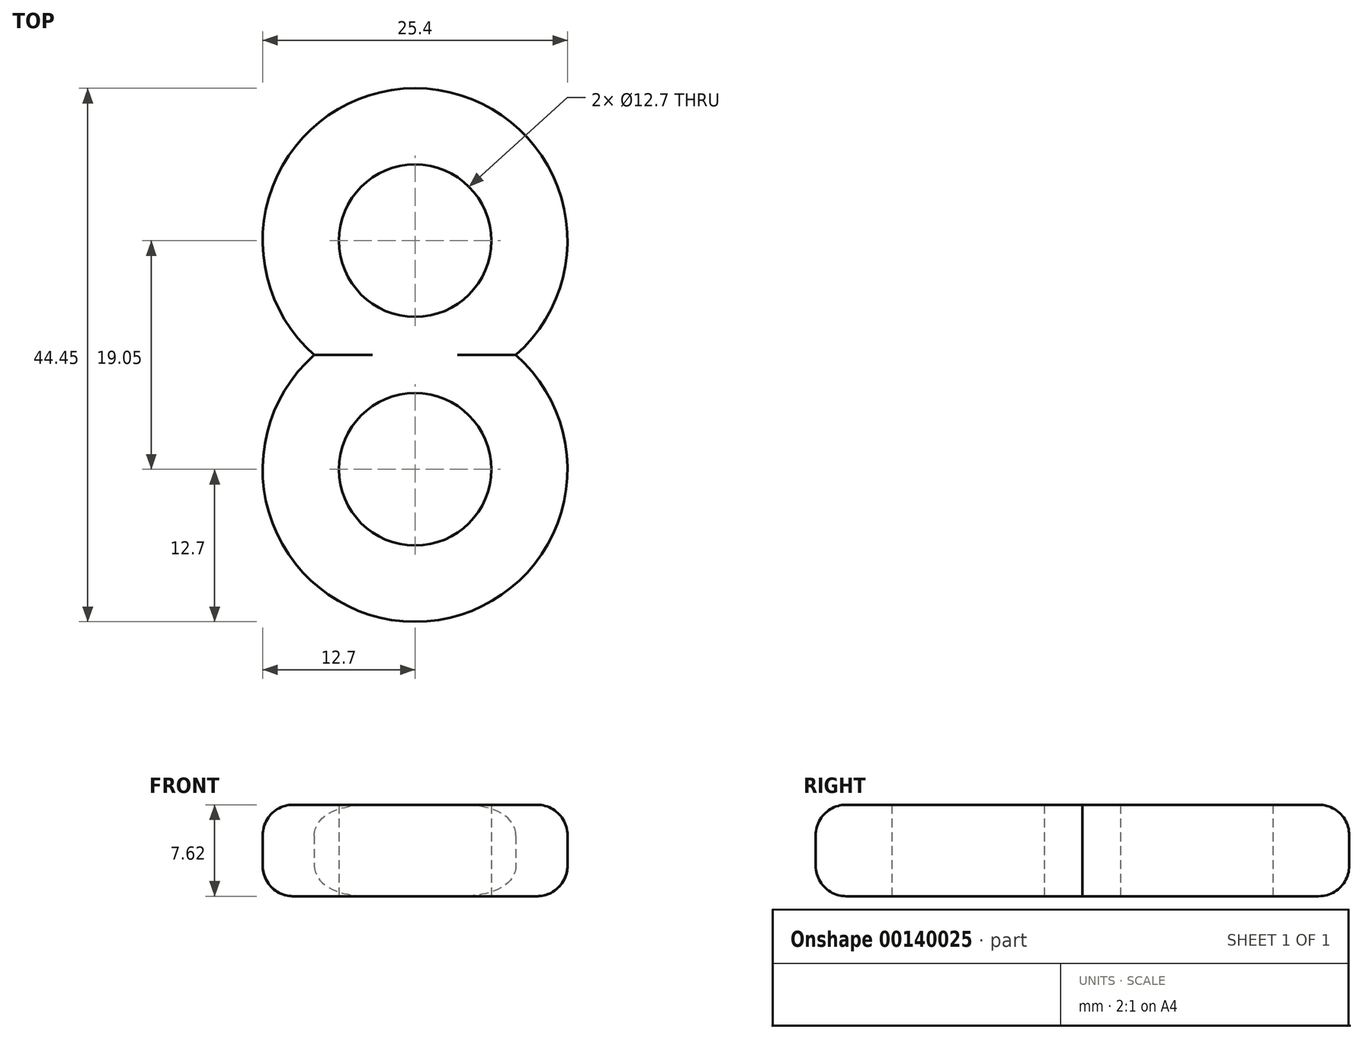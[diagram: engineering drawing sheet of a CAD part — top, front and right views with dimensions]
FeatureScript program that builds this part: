
annotation { "Feature Type Name" : "Feature", "Feature Type Description" : "" }
export const myFeature = defineFeature(function(context is Context, id is Id, definition is map)
    precondition{}
    {
        {
            var Q0;
            Q0=qCreatedBy(makeId("Top.planeOp"),FACE);
            var sketch = newSketch(context, id + "F0", { "sketchPlane" : qUnion([Q0])});
            skLineSegment(sketch, "E0", {"start": v(0, 25.4) * mm, "end": v(0, 0) * mm, "construction": true});
            skLineSegment(sketch, "E1", {"start": v(0, 0) * mm, "end": v(0, -25.4) * mm, "construction": true});
            skLineSegment(sketch, "E2", {"start": v(-25.4, 0) * mm, "end": v(-11, 0) * mm, "construction": true});
            skLineSegment(sketch, "E3", {"start": v(11, 0) * mm, "end": v(25.4, 0) * mm, "construction": true});
            skArc(sketch, "E4", {"start": v(8.4, 3.17) * mm, "mid": v(0, 25.4) * mm, "end": v(-8.4, 3.17) * mm});
            skArc(sketch, "E5", {"start": v(-8.4, 3.17) * mm, "mid": v(0, -19.05) * mm, "end": v(8.4, 3.17) * mm});
            skCircle(sketch, "E6.0", {"center": v(0, 12.7) * mm, "radius": 6.35 * mm});
            skCircle(sketch, "E7.0", {"center": v(0, -6.35) * mm, "radius": 6.35 * mm});
            skPoint(sketch, "E8.orphan", {"position": v(0, 0) * mm});
            skSolve(sketch);
        }
        {
            var Q0;
            Q0 = qSketchRegion(id + "F0", true);
            extrude(context, id + "F1", {"entities" : qUnion([Q0]), "depth" : 7.62 * mm});
        }
        {
            var Q0;
            Q0=makeQuery(id+"F1.opExtrude","CAP_EDGE",EDGE,{"disambiguationData":[OSD([sQuery(id+"F0.wireOp",EDGE,"E4")])],"isStart":false});
            var Q1;
            Q1=makeQuery(id+"F1.opExtrude","CAP_EDGE",EDGE,{"disambiguationData":[OSD([sQuery(id+"F0.wireOp",EDGE,"E5")])],"isStart":false});
            var Q2;
            Q2=makeQuery(id+"F1.opExtrude","CAP_EDGE",EDGE,{"disambiguationData":[OSD([sQuery(id+"F0.wireOp",EDGE,"E4")])],"isStart":true});
            var Q3;
            Q3=makeQuery(id+"F1.opExtrude","CAP_EDGE",EDGE,{"disambiguationData":[OSD([sQuery(id+"F0.wireOp",EDGE,"E5")])],"isStart":true});
            fillet(context, id + "F2", {"entities" : qUnion([Q0, Q1, Q2, Q3]), "radius" : 2.54 * mm, "tangentPropagation" : true, "allowEdgeOverflow" : false});
        }
    });
